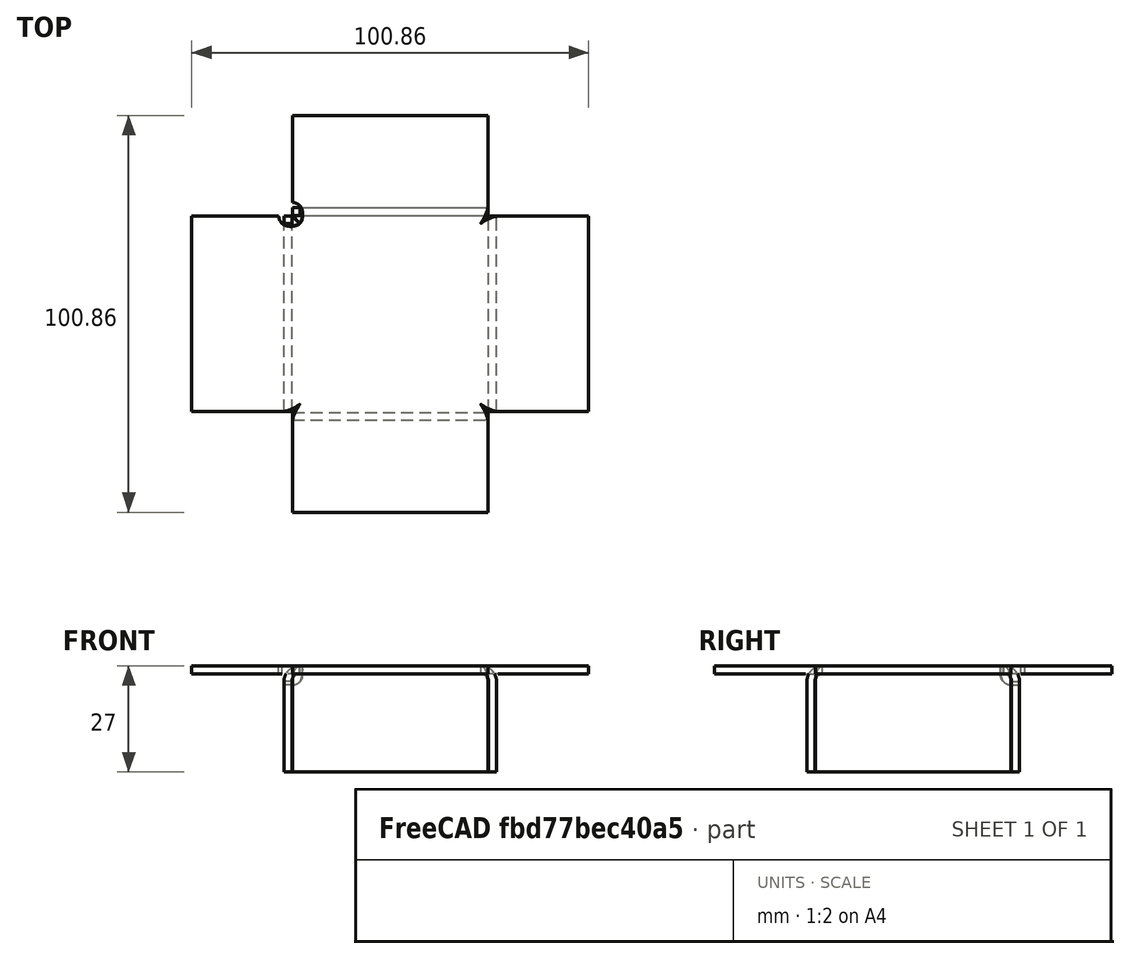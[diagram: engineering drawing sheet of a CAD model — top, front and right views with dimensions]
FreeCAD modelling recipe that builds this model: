
FCSTD DOCUMENT  (FreeCAD 0.19R20996 (Git))
Label: Round-Relief
License: All rights reserved
LicenseURL: www.visualprojections.com.au
objects: PartDesign::Fillet×2, Part::Box×1, PartDesign::FeatureBase×1, PartDesign::Body×1, Part::Sphere×1, Part::Cut×1, Part::FeaturePython×1, Part::Offset×1, Part::Feature×1, Sketcher::SketchObject×1
note: 13 computed .brp shape members not serialized (recipe doc carries the construction recipe); baked Part::Feature solids carry a one-line shape summary decoded from their .brp

FEATURE [Part::Box] Box  label="Cube"
  AttacherType = Attacher::AttachEngine3D
  Height = 25
  Length = 50
  Width = 50
FEATURE [PartDesign::FeatureBase] BaseFeature
  BaseFeature = -> Box
FEATURE [PartDesign::Fillet] Fillet
  Base = -> BaseFeature [Edge2,Edge10,Edge6,Edge12]
  BaseFeature = -> BaseFeature
  Radius = 2
  SupportTransform = true
FEATURE [PartDesign::Fillet] Fillet001
  Base = -> Fillet [Edge1,Edge5,Edge13,Edge4]
  BaseFeature = -> Fillet
  Radius = 0.2
  SupportTransform = true
FEATURE [PartDesign::Body] Body
  BaseFeature = -> Box
  Group = -> [BaseFeature,Fillet,Fillet001]
  Origin = -> Origin
  Tip = -> Fillet001
FEATURE [Part::Sphere] Sphere
  Angle1 = -90
  Angle2 = 90
  Angle3 = 360
  AttacherType = Attacher::AttachEngine3D
  Placement = pos=(0,50,25) rot=(0,0,1;0rad)
  Radius = 2.9
FEATURE [Part::Cut] Cut
  Base = -> Fillet001
  Tool = -> Sphere
FEATURE [Part::FeaturePython] Facebinder  # WARN: FeaturePython — macro-defined, semantics opaque (R4)
  Extrusion = 0
  Faces = -> [Cut]
  RemoveSplitter = false
  Sew = false
FEATURE [Part::Offset] Offset
  Fill = true
  Intersection = false
  Join = 0
  Mode = 0
  SelfIntersection = false
  Source = -> Facebinder
  Value = 2
FEATURE [Part::Feature] Unfold
  shape: bbox 100.9 x 100.9 x 2.201 mm, 25 faces (baked)
FEATURE [Sketcher::SketchObject] Sketch  label="Unfold_Sketch"
  Placement = pos=(0,0,27) rot=(0,0,1;0rad)
  sketch-geometry (52):
    g0: LineSegment StartX=49.8 StartY=-25.4296 StartZ=0 EndX=49.8 EndY=-2.42965 EndZ=0
    g1: LineSegment StartX=0.2 StartY=-25.4296 StartZ=0 EndX=49.8 EndY=-25.4296 EndZ=0
    g2: LineSegment StartX=0.2 StartY=-25.4296 StartZ=0 EndX=0.2 EndY=-2.42965 EndZ=0
    g3: BSplineCurve PolesCount=15 KnotsCount=13 Degree=3 IsPeriodic=0
    g4: BSplineCurve PolesCount=15 KnotsCount=13 Degree=3 IsPeriodic=0
    g5: BSplineCurve PolesCount=15 KnotsCount=13 Degree=3 IsPeriodic=0
    g6: BSplineCurve PolesCount=15 KnotsCount=13 Degree=3 IsPeriodic=0
    g7: BSplineCurve PolesCount=15 KnotsCount=13 Degree=3 IsPeriodic=0
    g8: BSplineCurve PolesCount=15 KnotsCount=13 Degree=3 IsPeriodic=0
    g9: BSplineCurve PolesCount=15 KnotsCount=13 Degree=3 IsPeriodic=0
    g10: BSplineCurve PolesCount=15 KnotsCount=13 Degree=3 IsPeriodic=0
    g11: BSplineCurve PolesCount=15 KnotsCount=13 Degree=3 IsPeriodic=0
    g12: ArcOfCircle CenterX=-0.429646 CenterY=50 CenterZ=0 NormalX=0 NormalY=0 NormalZ=1 AngleXU=0 Radius=2.9 StartAngle=3.21061 EndAngle=3.95138
    g13: LineSegment StartX=-25.4296 StartY=49.8 StartZ=0 EndX=-3.32274 EndY=49.8 EndZ=0
    g14: LineSegment StartX=-25.4296 StartY=0.2 StartZ=0 EndX=-25.4296 EndY=49.8 EndZ=0
    g15: LineSegment StartX=-25.4296 StartY=0.2 StartZ=0 EndX=-2.42965 EndY=0.2 EndZ=0
    g16: BSplineCurve PolesCount=15 KnotsCount=13 Degree=3 IsPeriodic=0
    g17: BSplineCurve PolesCount=15 KnotsCount=13 Degree=3 IsPeriodic=0
    g18: BSplineCurve PolesCount=15 KnotsCount=13 Degree=3 IsPeriodic=0
    g19: BSplineCurve PolesCount=15 KnotsCount=13 Degree=3 IsPeriodic=0
    g20: BSplineCurve PolesCount=15 KnotsCount=13 Degree=3 IsPeriodic=0
    g21: BSplineCurve PolesCount=15 KnotsCount=13 Degree=3 IsPeriodic=0
    g22: BSplineCurve PolesCount=15 KnotsCount=13 Degree=3 IsPeriodic=0
    g23: BSplineCurve PolesCount=15 KnotsCount=13 Degree=3 IsPeriodic=0
    g24: BSplineCurve PolesCount=15 KnotsCount=13 Degree=3 IsPeriodic=0
    g25: BSplineCurve PolesCount=15 KnotsCount=13 Degree=3 IsPeriodic=0
    g26: BSplineCurve PolesCount=15 KnotsCount=13 Degree=3 IsPeriodic=0
    g27: LineSegment StartX=75.4296 StartY=49.8 StartZ=0 EndX=52.4296 EndY=49.8 EndZ=0
    g28: LineSegment StartX=75.4296 StartY=0.2 StartZ=0 EndX=75.4296 EndY=49.8 EndZ=0
    g29: LineSegment StartX=75.4296 StartY=0.2 StartZ=0 EndX=52.4296 EndY=0.2 EndZ=0
    g30: BSplineCurve PolesCount=15 KnotsCount=13 Degree=3 IsPeriodic=0
    g31: BSplineCurve PolesCount=15 KnotsCount=13 Degree=3 IsPeriodic=0
    g32: BSplineCurve PolesCount=15 KnotsCount=13 Degree=3 IsPeriodic=0
    g33: BSplineCurve PolesCount=15 KnotsCount=13 Degree=3 IsPeriodic=0
    g34: BSplineCurve PolesCount=15 KnotsCount=13 Degree=3 IsPeriodic=0
    g35: BSplineCurve PolesCount=15 KnotsCount=13 Degree=3 IsPeriodic=0
    g36: BSplineCurve PolesCount=15 KnotsCount=13 Degree=3 IsPeriodic=0
    g37: BSplineCurve PolesCount=15 KnotsCount=13 Degree=3 IsPeriodic=0
    g38: ArcOfCircle CenterX=0 CenterY=50.4296 CenterZ=0 NormalX=0 NormalY=0 NormalZ=1 AngleXU=0 Radius=2.9 StartAngle=0.761013 EndAngle=1.50178
    g39: LineSegment StartX=0.2 StartY=75.4296 StartZ=0 EndX=0.2 EndY=53.3227 EndZ=0
    g40: LineSegment StartX=0.2 StartY=75.4296 StartZ=0 EndX=49.8 EndY=75.4296 EndZ=0
    g41: LineSegment StartX=49.8 StartY=75.4296 StartZ=0 EndX=49.8 EndY=52.4296 EndZ=0
    g42: BSplineCurve PolesCount=15 KnotsCount=13 Degree=3 IsPeriodic=0
    g43: BSplineCurve PolesCount=15 KnotsCount=13 Degree=3 IsPeriodic=0
    g44: BSplineCurve PolesCount=15 KnotsCount=13 Degree=3 IsPeriodic=0
    g45: BSplineCurve PolesCount=15 KnotsCount=13 Degree=3 IsPeriodic=0
    g46: BSplineCurve PolesCount=15 KnotsCount=13 Degree=3 IsPeriodic=0
    g47: ArcOfCircle CenterX=0 CenterY=50 CenterZ=0 NormalX=0 NormalY=0 NormalZ=1 AngleXU=0 Radius=2.9 StartAngle=5.4734 EndAngle=5.52217
    g48: LineSegment StartX=-0.214823 StartY=0.72726 StartZ=0 EndX=-0.214823 EndY=47.2209 EndZ=0
    g49: LineSegment StartX=2.77907 StartY=50.2148 StartZ=0 EndX=49.2727 EndY=50.2148 EndZ=0
    g50: LineSegment StartX=50.2148 StartY=0.72726 StartZ=0 EndX=50.2148 EndY=49.2727 EndZ=0
    g51: LineSegment StartX=0.72726 StartY=-0.214823 StartZ=0 EndX=49.2727 EndY=-0.214823 EndZ=0
